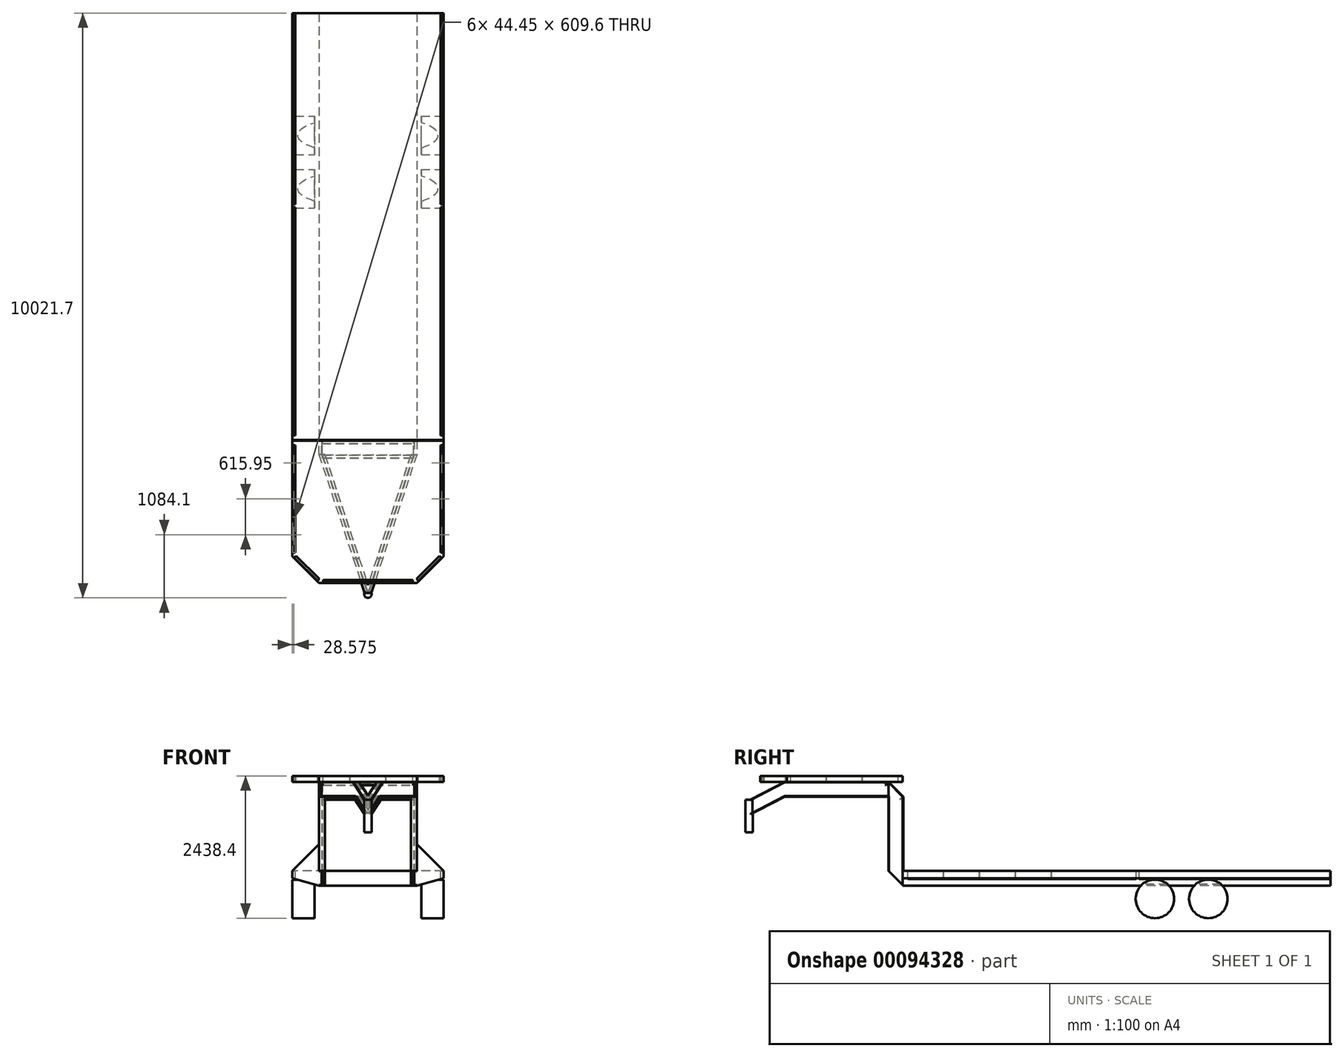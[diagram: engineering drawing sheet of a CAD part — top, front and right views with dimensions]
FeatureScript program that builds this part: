
annotation { "Feature Type Name" : "Feature", "Feature Type Description" : "" }
export const myFeature = defineFeature(function(context is Context, id is Id, definition is map)
    precondition{}
    {
        {
            var Q0;
            Q0=qCreatedBy(makeId("Front.planeOp"),FACE);
            var sketch = newSketch(context, id + "F0", { "sketchPlane" : qUnion([Q0])});
            skLineSegment(sketch, "E0.rect.bottom", {"start": v(1295.4, 812.8) * mm, "end": v(-1295.4, 812.8) * mm});
            skLineSegment(sketch, "E0.rect.top", {"start": v(1295.4, 558.8) * mm, "end": v(-1295.4, 558.8) * mm});
            skLineSegment(sketch, "E0.rect.left", {"start": v(1295.4, 812.8) * mm, "end": v(1295.4, 558.8) * mm});
            skLineSegment(sketch, "E0.rect.right", {"start": v(-1295.4, 812.8) * mm, "end": v(-1295.4, 558.8) * mm});
            skPoint(sketch, "E0.rect.middle", {"position": v(0, 685.8) * mm});
            skSolve(sketch);
        }
        {
            var Q0;
            Q0=qSketchRegion(id+"F0",true);
            extrude(context, id + "F1", {"entities" : qUnion([Q0]), "depth" : 7315.2 * mm});
        }
        {
            var Q0;
            {var subQ0=sQuery(id+"FU6Cp20yWSytbLJ_1.wireOp",EDGE,"516zEHSR-i4bq-akFn-s86x-5tDhRc9qmYIe");var subQ1=sQuery(id+"FU6Cp20yWSytbLJ_1.wireOp",EDGE,"pIKuKbnO-BRQA-nErB-13iL-2qYtMzEWX1Er");var subQ2=sQuery(id+"FU6Cp20yWSytbLJ_1.wireOp",EDGE,"PYxLWf9Y-Gqo5-IOfk-YQH7-kY8rKgNUq3Ly");var subQ3=sQuery(id+"FU6Cp20yWSytbLJ_1.wireOp",EDGE,"HUdA5PYD-mE7W-SRS9-FlNJ-WsRSMuGNaLoF");var subQ4=makeQuery(id+"FC5x2sPdwrUGjzl_1.opExtrude","CAP_FACE",FACE,{"disambiguationData":[OSD([subQ3,subQ2,subQ1,subQ0])],"isStart":true});var subQ5=sQuery(id+"FtYi234e1mes3no_1.wireOp",EDGE,"0333ae5e-be5c-4696-89fa-82c44326a229");var subQ6=makeQuery(id+"Fx2GEeHIH9ebrkq_1.opExtrude","CAP_FACE",FACE,{"disambiguationData":[OSD([subQ5])],"isStart":true});var subQ7=sQuery(id+"F0.wireOp",EDGE,"E0.rect.right");var subQ8=makeQuery(id+"FC5x2sPdwrUGjzl_1.opExtrude","CAP_FACE",FACE,{"disambiguationData":[OSD([subQ7])],"isStart":false});var subQ9=makeQuery(id+"F1.opExtrude","SWEPT_FACE",FACE,{"disambiguationData":[OSD([subQ7])]});var subQ10=sQuery(id+"FtYi234e1mes3no_1.wireOp",EDGE,"dfd4e7ae-838f-45d7-bc5a-27b7e8f56e23");var subQ11=sQuery(id+"F0.wireOp",EDGE,"E0.rect.left");var subQ12=makeQuery(id+"Fx2GEeHIH9ebrkq_1.opExtrude","CAP_FACE",FACE,{"disambiguationData":[OSD([subQ11,subQ3,subQ2,subQ1,subQ0]),ownerDisambiguation([makeQuery(id+"Fx2GEeHIH9ebrkq_1.opExtrude","SWEPT_BODY",BODY,{"disambiguationData":[OSD([subQ10])]})])],"isStart":false});var subQ13=makeQuery(id+"F1.opExtrude","SWEPT_FACE",FACE,{"disambiguationData":[OSD([subQ11])]});var subQ14=makeQuery(id+"Fx2GEeHIH9ebrkq_1.opExtrude","SWEPT_FACE",FACE,{"disambiguationData":[OSD([subQ5])]});var subQ15=makeQuery(id+"Fx2GEeHIH9ebrkq_1.opExtrude","CAP_FACE",FACE,{"disambiguationData":[OSD([subQ11,subQ3,subQ2,subQ1,subQ0]),ownerDisambiguation([makeQuery(id+"Fx2GEeHIH9ebrkq_1.opExtrude","SWEPT_BODY",BODY,{"disambiguationData":[OSD([subQ5])]})])],"isStart":false});var subQ16=makeQuery(id+"Fx2GEeHIH9ebrkq_1.opExtrude","SWEPT_FACE",FACE,{"disambiguationData":[OSD([subQ10])]});var subQ17=makeQuery(id+"Fx2GEeHIH9ebrkq_1.opExtrude","CAP_FACE",FACE,{"disambiguationData":[OSD([subQ10])],"isStart":true});var subQ18=sQuery(id+"F0.wireOp",EDGE,"E0.rect.top");var subQ19=makeQuery(id+"F1.opExtrude","SWEPT_FACE",FACE,{"disambiguationData":[OSD([subQ18])]});var subQ20=sQuery(id+"F0.wireOp",EDGE,"E0.rect.bottom");Q0=makeQuery(id+"FWcp0c4Uuyueshzcz_1.boolean.opBoolean","MERGE",FACE,{"derivedFrom":[makeQuery(id+"Fx2GEeHIH9ebrkq_1.boolean.opBoolean","SPLIT",FACE,{"disambiguationData":[TD([makeQuery(id+"F1.opExtrude","CAP_FACE",FACE,{"disambiguationData":[OSD([subQ20,subQ18,subQ11,subQ7])],"isStart":true}),subQ13,subQ9,subQ8,subQ4,subQ16,subQ17,subQ6,subQ12,subQ15])],"derivedFrom":subQ19}),makeQuery(id+"Fx2GEeHIH9ebrkq_1.boolean.opBoolean","SPLIT",FACE,{"disambiguationData":[TD([makeQuery(id+"F1.opExtrude","CAP_FACE",FACE,{"disambiguationData":[OSD([subQ20,subQ18,subQ11,subQ7])],"isStart":false}),subQ13,subQ9,subQ8,subQ4,subQ17,subQ14,subQ6,subQ12,subQ15])],"derivedFrom":subQ19}),makeQuery(id+"Fx2GEeHIH9ebrkq_1.boolean.opBoolean","SPLIT",FACE,{"disambiguationData":[TD([subQ13,subQ9,subQ8,subQ4,subQ16,subQ17,subQ14,subQ6,subQ12,subQ15])],"derivedFrom":subQ19}),makeQuery(id+"FWcp0c4Uuyueshzcz_1.opExtrude","SWEPT_FACE",FACE,{"disambiguationData":[OSD([sQuery(id+"FtVBCKT4kURnRFX_1.wireOp",EDGE,"0c15b902-9fc4-4e75-a3e0-c7f493582f48.bottom")])]})]});}
            var sketch = newSketch(context, id + "F2", { "sketchPlane" : qUnion([Q0])});
            skLineSegment(sketch, "E1", {"start": v(838.2, 7315.2) * mm, "end": v(838.2, 7324.72) * mm});
            skLineSegment(sketch, "E2", {"start": v(838.2, 7324.72) * mm, "end": v(792.16, 7324.72) * mm});
            skLineSegment(sketch, "E3", {"start": v(792.16, 7324.72) * mm, "end": v(792.16, 7559.68) * mm});
            skLineSegment(sketch, "E4", {"start": v(792.16, 7559.68) * mm, "end": v(838.2, 7559.68) * mm});
            skLineSegment(sketch, "E5", {"start": v(838.2, 7559.68) * mm, "end": v(838.2, 7569.2) * mm});
            skLineSegment(sketch, "E6", {"start": v(838.2, 7569.2) * mm, "end": v(736.6, 7569.2) * mm});
            skLineSegment(sketch, "E7", {"start": v(736.6, 7569.2) * mm, "end": v(736.6, 7559.68) * mm});
            skLineSegment(sketch, "E8", {"start": v(736.6, 7559.68) * mm, "end": v(782.64, 7559.68) * mm});
            skLineSegment(sketch, "E9", {"start": v(782.64, 7559.68) * mm, "end": v(782.64, 7324.72) * mm});
            skLineSegment(sketch, "E10", {"start": v(782.64, 7324.72) * mm, "end": v(736.6, 7324.72) * mm});
            skLineSegment(sketch, "E11", {"start": v(736.6, 7324.72) * mm, "end": v(736.6, 7315.2) * mm});
            skLineSegment(sketch, "E12", {"start": v(736.6, 7315.2) * mm, "end": v(838.2, 7315.2) * mm});
            skLineSegment(sketch, "E13", {"start": v(792.16, 7559.68) * mm, "end": v(782.64, 7559.68) * mm, "construction": true});
            skLineSegment(sketch, "E14", {"start": v(0, 7315.2) * mm, "end": v(0, 0) * mm, "construction": true});
            skLineSegment(sketch, "E15.MirrorCS", {"start": v(-792.16, 7559.68) * mm, "end": v(-782.64, 7559.68) * mm, "construction": true});
            skLineSegment(sketch, "E16.MirrorCS", {"start": v(-736.6, 7559.68) * mm, "end": v(-782.64, 7559.68) * mm});
            skLineSegment(sketch, "E17.MirrorCS", {"start": v(-736.6, 7569.2) * mm, "end": v(-736.6, 7559.68) * mm});
            skLineSegment(sketch, "E18.MirrorCS", {"start": v(-838.2, 7315.2) * mm, "end": v(-838.2, 7324.72) * mm});
            skLineSegment(sketch, "E19.MirrorCS", {"start": v(-792.16, 7559.68) * mm, "end": v(-838.2, 7559.68) * mm});
            skLineSegment(sketch, "E20.MirrorCS", {"start": v(-838.2, 7559.68) * mm, "end": v(-838.2, 7569.2) * mm});
            skLineSegment(sketch, "E21.MirrorCS", {"start": v(-838.2, 7569.2) * mm, "end": v(-736.6, 7569.2) * mm});
            skLineSegment(sketch, "E22.MirrorCS", {"start": v(-736.6, 7315.2) * mm, "end": v(-838.2, 7315.2) * mm});
            skLineSegment(sketch, "E23.MirrorCS", {"start": v(-736.6, 7324.72) * mm, "end": v(-736.6, 7315.2) * mm});
            skLineSegment(sketch, "E24.MirrorCS", {"start": v(-838.2, 7324.72) * mm, "end": v(-792.16, 7324.72) * mm});
            skLineSegment(sketch, "E25.MirrorCS", {"start": v(-782.64, 7324.72) * mm, "end": v(-736.6, 7324.72) * mm});
            skLineSegment(sketch, "E26.MirrorCS", {"start": v(-792.16, 7324.72) * mm, "end": v(-792.16, 7559.68) * mm});
            skLineSegment(sketch, "E27.MirrorCS", {"start": v(-782.64, 7559.68) * mm, "end": v(-782.64, 7324.72) * mm});
            skSolve(sketch);
        }
        {
            var Q0;
            Q0=makeQuery(id+"F2.imprint","IMPRINT",FACE,{"disambiguationData":[TD([[makeQuery(id+"F2.imprint","IMPRINT",EDGE,{"derivedFrom":sQuery(id+"F2.wireOp",EDGE,"E16.MirrorCS")}),-1.0]])]});
            var Q1;
            Q1=makeQuery(id+"F2.imprint","IMPRINT",FACE,{"disambiguationData":[TD([[makeQuery(id+"F2.imprint","IMPRINT",EDGE,{"derivedFrom":sQuery(id+"F2.wireOp",EDGE,"E1")}),1.0]])]});
            extrude(context, id + "F3", {"entities" : qUnion([Q0, Q1]), "operationType" : NewBodyOperationType.ADD, "oppositeDirection" : true, "depth" : 1524 * mm});
        }
        {
            var Q0;
            Q0=makeQuery(id+"F3.opExtrude","CAP_FACE",FACE,{"disambiguationData":[OSD([sQuery(id+"F2.wireOp",EDGE,"E1"),sQuery(id+"F2.wireOp",EDGE,"E2"),sQuery(id+"F2.wireOp",EDGE,"E3"),sQuery(id+"F2.wireOp",EDGE,"E4"),sQuery(id+"F2.wireOp",EDGE,"E5"),sQuery(id+"F2.wireOp",EDGE,"E6"),sQuery(id+"F2.wireOp",EDGE,"E7"),sQuery(id+"F2.wireOp",EDGE,"E8"),sQuery(id+"F2.wireOp",EDGE,"E9"),sQuery(id+"F2.wireOp",EDGE,"E10"),sQuery(id+"F2.wireOp",EDGE,"E11"),sQuery(id+"F2.wireOp",EDGE,"E12")])],"isStart":false});
            var sketch = newSketch(context, id + "F4", { "sketchPlane" : qUnion([Q0])});
            skLineSegment(sketch, "E28", {"start": v(-787.4, -7569.2) * mm, "end": v(-201.04, -9347.2) * mm});
            skLineSegment(sketch, "E29", {"start": v(-201.04, -9347.2) * mm, "end": v(0, -9956.8) * mm});
            skLineSegment(sketch, "E30", {"start": v(0, -9956.8) * mm, "end": v(201.04, -9347.2) * mm});
            skLineSegment(sketch, "E31", {"start": v(201.04, -9347.2) * mm, "end": v(787.4, -7569.2) * mm});
            skSolve(sketch);
        }
        {
            var Q0;
            {var subQ0=sQuery(id+"FU6Cp20yWSytbLJ_1.wireOp",EDGE,"pIKuKbnO-BRQA-nErB-13iL-2qYtMzEWX1Er");var subQ1=sQuery(id+"FU6Cp20yWSytbLJ_1.wireOp",EDGE,"PYxLWf9Y-Gqo5-IOfk-YQH7-kY8rKgNUq3Ly");var subQ2=sQuery(id+"FU6Cp20yWSytbLJ_1.wireOp",EDGE,"HUdA5PYD-mE7W-SRS9-FlNJ-WsRSMuGNaLoF");var subQ3=sQuery(id+"F0.wireOp",EDGE,"E0.rect.bottom");var subQ5=sQuery(id+"F0.wireOp",EDGE,"E0.rect.left");var subQ7=sQuery(id+"FU6Cp20yWSytbLJ_1.wireOp",EDGE,"516zEHSR-i4bq-akFn-s86x-5tDhRc9qmYIe");Q0=makeQuery(id+"FsKg1WZKStzT7it_1.boolean.opBoolean","SPLIT",FACE,{"disambiguationData":[TD([makeQuery(id+"F1.opExtrude","SWEPT_FACE",FACE,{"disambiguationData":[OSD([subQ3])]})])],"derivedFrom":makeQuery(id+"Fx2GEeHIH9ebrkq_1.boolean.opBoolean","MERGE",FACE,{"derivedFrom":[makeQuery(id+"FC5x2sPdwrUGjzl_1.boolean.opBoolean","MERGE",FACE,{"derivedFrom":[makeQuery(id+"F1.opExtrude","SWEPT_FACE",FACE,{"disambiguationData":[OSD([subQ5])]}),makeQuery(id+"FC5x2sPdwrUGjzl_1.opExtrude","CAP_FACE",FACE,{"disambiguationData":[OSD([subQ2,subQ1,subQ0,subQ7])],"isStart":true})]}),makeQuery(id+"Fx2GEeHIH9ebrkq_1.opExtrude","CAP_FACE",FACE,{"disambiguationData":[OSD([subQ5,subQ2,subQ1,subQ0,subQ7]),ownerDisambiguation([makeQuery(id+"Fx2GEeHIH9ebrkq_1.opExtrude","SWEPT_BODY",BODY,{"disambiguationData":[OSD([sQuery(id+"FtYi234e1mes3no_1.wireOp",EDGE,"dfd4e7ae-838f-45d7-bc5a-27b7e8f56e23")])]})])],"isStart":false}),makeQuery(id+"Fx2GEeHIH9ebrkq_1.opExtrude","CAP_FACE",FACE,{"disambiguationData":[OSD([subQ5,subQ2,subQ1,subQ0,subQ7]),ownerDisambiguation([makeQuery(id+"Fx2GEeHIH9ebrkq_1.opExtrude","SWEPT_BODY",BODY,{"disambiguationData":[OSD([sQuery(id+"FtYi234e1mes3no_1.wireOp",EDGE,"0333ae5e-be5c-4696-89fa-82c44326a229")])]})])],"isStart":false})]})});}
            var sketch = newSketch(context, id + "F5", { "sketchPlane" : qUnion([Q0])});
            skLineSegment(sketch, "E32", {"start": v(-7315.2, 558.8) * mm, "end": v(-7569.2, 812.8) * mm});
            skLineSegment(sketch, "E33", {"start": v(-7569.2, 812.8) * mm, "end": v(-7569.2, 558.8) * mm});
            skLineSegment(sketch, "E34", {"start": v(-7569.2, 558.8) * mm, "end": v(-7315.2, 558.8) * mm});
            skSolve(sketch);
        }
        {
            var Q0;
            Q0=makeQuery(id+"F5.imprint","IMPRINT",FACE,{"disambiguationData":[TD([[makeQuery(id+"F5.imprint","IMPRINT",EDGE,{"derivedFrom":sQuery(id+"F5.wireOp",EDGE,"E32")}),1.0]])]});
            extrude(context, id + "F6", {"entities" : qUnion([Q0]), "operationType" : NewBodyOperationType.REMOVE, "endBound" : BoundingType.THROUGH_ALL, "oppositeDirection" : true, "depth" : 25.4 * mm});
        }
        {
            var Q0;
            Q0=makeQuery(id+"F3.opExtrude","SWEPT_FACE",FACE,{"disambiguationData":[OSD([sQuery(id+"F2.wireOp",EDGE,"E6")])]});
            var sketch = newSketch(context, id + "F7", { "sketchPlane" : qUnion([Q0])});
            skLineSegment(sketch, "E35", {"start": v(736.6, 2082.8) * mm, "end": v(838.2, 2082.8) * mm});
            skLineSegment(sketch, "E36", {"start": v(838.2, 2082.8) * mm, "end": v(838.2, 2092.32) * mm});
            skLineSegment(sketch, "E37", {"start": v(838.2, 2092.32) * mm, "end": v(792.16, 2092.32) * mm});
            skLineSegment(sketch, "E38", {"start": v(792.16, 2092.32) * mm, "end": v(792.16, 2327.28) * mm});
            skLineSegment(sketch, "E39", {"start": v(792.16, 2327.28) * mm, "end": v(838.2, 2327.28) * mm});
            skLineSegment(sketch, "E40", {"start": v(838.2, 2327.28) * mm, "end": v(838.2, 2336.8) * mm});
            skLineSegment(sketch, "E41", {"start": v(838.2, 2336.8) * mm, "end": v(736.6, 2336.8) * mm});
            skLineSegment(sketch, "E42", {"start": v(736.6, 2336.8) * mm, "end": v(736.6, 2327.28) * mm});
            skLineSegment(sketch, "E43", {"start": v(736.6, 2327.28) * mm, "end": v(782.64, 2327.28) * mm});
            skLineSegment(sketch, "E44", {"start": v(782.64, 2327.28) * mm, "end": v(782.64, 2092.32) * mm});
            skLineSegment(sketch, "E45", {"start": v(782.64, 2092.32) * mm, "end": v(736.6, 2092.32) * mm});
            skLineSegment(sketch, "E46", {"start": v(736.6, 2092.32) * mm, "end": v(736.6, 2082.8) * mm});
            skLineSegment(sketch, "E47", {"start": v(782.64, 2092.32) * mm, "end": v(792.16, 2092.32) * mm, "construction": true});
            skLineSegment(sketch, "E48", {"start": v(0, 558.8) * mm, "end": v(0, 812.8) * mm, "construction": true});
            skLineSegment(sketch, "E49.MirrorCS", {"start": v(-782.64, 2092.32) * mm, "end": v(-792.16, 2092.32) * mm, "construction": true});
            skLineSegment(sketch, "E50.MirrorCS", {"start": v(-782.64, 2092.32) * mm, "end": v(-736.6, 2092.32) * mm});
            skLineSegment(sketch, "E51.MirrorCS", {"start": v(-736.6, 2092.32) * mm, "end": v(-736.6, 2082.8) * mm});
            skLineSegment(sketch, "E52.MirrorCS", {"start": v(-736.6, 2082.8) * mm, "end": v(-838.2, 2082.8) * mm});
            skLineSegment(sketch, "E53.MirrorCS", {"start": v(-838.2, 2082.8) * mm, "end": v(-838.2, 2092.32) * mm});
            skLineSegment(sketch, "E54.MirrorCS", {"start": v(-838.2, 2092.32) * mm, "end": v(-792.16, 2092.32) * mm});
            skLineSegment(sketch, "E55.MirrorCS", {"start": v(-792.16, 2327.28) * mm, "end": v(-838.2, 2327.28) * mm});
            skLineSegment(sketch, "E56.MirrorCS", {"start": v(-838.2, 2336.8) * mm, "end": v(-736.6, 2336.8) * mm});
            skLineSegment(sketch, "E57.MirrorCS", {"start": v(-736.6, 2327.28) * mm, "end": v(-782.64, 2327.28) * mm});
            skLineSegment(sketch, "E58.MirrorCS", {"start": v(-736.6, 2336.8) * mm, "end": v(-736.6, 2327.28) * mm});
            skLineSegment(sketch, "E59.MirrorCS", {"start": v(-838.2, 2327.28) * mm, "end": v(-838.2, 2336.8) * mm});
            skLineSegment(sketch, "E60.MirrorCS", {"start": v(-792.16, 2092.32) * mm, "end": v(-792.16, 2327.28) * mm});
            skLineSegment(sketch, "E61.MirrorCS", {"start": v(-782.64, 2327.28) * mm, "end": v(-782.64, 2092.32) * mm});
            skSolve(sketch);
        }
        {
            var Q1;
            Q1=makeQuery(id+"F4.imprint","IMPRINT",FACE,{"disambiguationData":[TD([[makeQuery(id+"F4.imprint","IMPRINT",EDGE,{"derivedFrom":makeQuery(id+"F3.opExtrude","CAP_EDGE",EDGE,{"disambiguationData":[OSD([sQuery(id+"F2.wireOp",EDGE,"E1")])],"isStart":false})}),-1.0]])]});
            var Q2;
            Q2=makeQuery(id+"F7.imprint","IMPRINT",FACE,{"disambiguationData":[TD([[makeQuery(id+"F7.imprint","IMPRINT",EDGE,{"derivedFrom":sQuery(id+"F7.wireOp",EDGE,"E35")}),-1.0]])]});
            var Q3;
            Q3=sQuery(id+"F7.wireOp",VERTEX,"E45.end");
            var Q4;
            Q4=makeQuery(id+"F3.opExtrude","CAP_VERTEX",VERTEX,{"disambiguationData":[OSD([sQuery(id+"F2.wireOp",EDGE,"E7"),sQuery(id+"F2.wireOp",EDGE,"E8")])],"isStart":false});
            loft(context, id + "F8", {"operationType" : NewBodyOperationType.ADD, "sheetProfilesArray" : [{ "sheetProfileEntities" : qUnion([Q1]) }, { "sheetProfileEntities" : qUnion([Q2]) }], "matchConnections" : true, "connections" : [{ "connectionEntities" : qUnion([Q3, Q4]), "connectionEdgeQueries" : qUnion([]), "connectionEdgeParameters" : [] }]});
        }
        {
            var Q1;
            Q1=makeQuery(id+"F7.imprint","IMPRINT",FACE,{"disambiguationData":[TD([[makeQuery(id+"F7.imprint","IMPRINT",EDGE,{"derivedFrom":sQuery(id+"F7.wireOp",EDGE,"E50.MirrorCS")}),-1.0]])]});
            var Q2;
            Q2=makeQuery(id+"F3.opExtrude","CAP_FACE",FACE,{"disambiguationData":[OSD([sQuery(id+"F2.wireOp",EDGE,"E16.MirrorCS"),sQuery(id+"F2.wireOp",EDGE,"E17.MirrorCS"),sQuery(id+"F2.wireOp",EDGE,"E18.MirrorCS"),sQuery(id+"F2.wireOp",EDGE,"E19.MirrorCS"),sQuery(id+"F2.wireOp",EDGE,"E20.MirrorCS"),sQuery(id+"F2.wireOp",EDGE,"E21.MirrorCS"),sQuery(id+"F2.wireOp",EDGE,"E22.MirrorCS"),sQuery(id+"F2.wireOp",EDGE,"E23.MirrorCS"),sQuery(id+"F2.wireOp",EDGE,"E24.MirrorCS"),sQuery(id+"F2.wireOp",EDGE,"E25.MirrorCS"),sQuery(id+"F2.wireOp",EDGE,"E26.MirrorCS"),sQuery(id+"F2.wireOp",EDGE,"E27.MirrorCS")])],"isStart":false});
            loft(context, id + "F9", {"operationType" : NewBodyOperationType.ADD, "sheetProfilesArray" : [{ "sheetProfileEntities" : qUnion([Q1]) }, { "sheetProfileEntities" : qUnion([Q2]) }]});
        }
        {
            var Q0;
            Q0=qSketchRegion(id+"F4",true);
            var Q1;
            Q1=makeQuery(id+"F7.imprint","IMPRINT",FACE,{"disambiguationData":[TD([[makeQuery(id+"F7.imprint","IMPRINT",EDGE,{"derivedFrom":sQuery(id+"F7.wireOp",EDGE,"E35")}),-1.0]])]});
            var Q2;
            Q2=sQuery(id+"F4.wireOp",EDGE,"E31");
            sweep(context, id + "F10", {"operationType" : NewBodyOperationType.ADD, "profiles" : qUnion([Q0, Q1]), "path" : qUnion([Q2]), "keepProfileOrientation" : true});
        }
        {
            var Q0;
            Q0=makeQuery(id+"F7.imprint","IMPRINT",FACE,{"disambiguationData":[TD([[makeQuery(id+"F7.imprint","IMPRINT",EDGE,{"derivedFrom":sQuery(id+"F7.wireOp",EDGE,"E50.MirrorCS")}),-1.0]])]});
            var Q1;
            Q1=sQuery(id+"F4.wireOp",EDGE,"E28");
            sweep(context, id + "F11", {"operationType" : NewBodyOperationType.ADD, "profiles" : qUnion([Q0]), "path" : qUnion([Q1]), "keepProfileOrientation" : true});
        }
        {
            var Q0;
            Q0=makeQuery(id+"F10.opSweep","SWEPT_FACE",FACE,{"disambiguationData":[OSD([sQuery(id+"F4.wireOp",EDGE,"E31"),sQuery(id+"F7.wireOp",EDGE,"E38")])]});
            var sketch = newSketch(context, id + "F12", { "sketchPlane" : qUnion([Q0])});
            skLineSegment(sketch, "E62", {"start": v(-8812.47, 2092.32) * mm, "end": v(-9455.86, 1778) * mm});
            skSolve(sketch);
        }
        {
            var Q0;
            Q0=makeQuery(id+"F10.opSweep","CAP_FACE",FACE,{"disambiguationData":[OSD([sQuery(id+"F4.wireOp",VERTEX,"E31.start"),sQuery(id+"F7.wireOp",EDGE,"E35"),sQuery(id+"F7.wireOp",EDGE,"E36"),sQuery(id+"F7.wireOp",EDGE,"E37"),sQuery(id+"F7.wireOp",EDGE,"E38"),sQuery(id+"F7.wireOp",EDGE,"E39"),sQuery(id+"F7.wireOp",EDGE,"E40"),sQuery(id+"F7.wireOp",EDGE,"E41"),sQuery(id+"F7.wireOp",EDGE,"E42"),sQuery(id+"F7.wireOp",EDGE,"E43"),sQuery(id+"F7.wireOp",EDGE,"E44"),sQuery(id+"F7.wireOp",EDGE,"E45"),sQuery(id+"F7.wireOp",EDGE,"E46")])],"isStart":false});
            var Q1;
            Q1=sQuery(id+"F12.wireOp",EDGE,"E62");
            sweep(context, id + "F13", {"operationType" : NewBodyOperationType.ADD, "profiles" : qUnion([Q0]), "path" : qUnion([Q1])});
        }
        {
            var Q0;
            Q0=makeQuery(id+"F11.opSweep","SWEPT_FACE",FACE,{"disambiguationData":[OSD([sQuery(id+"F4.wireOp",EDGE,"E28"),sQuery(id+"F7.wireOp",EDGE,"E60.MirrorCS")])]});
            var sketch = newSketch(context, id + "F14", { "sketchPlane" : qUnion([Q0])});
            skLineSegment(sketch, "E63", {"start": v(8812.47, 2092.32) * mm, "end": v(9455.86, 1778) * mm});
            skSolve(sketch);
        }
        {
            var Q0;
            Q0=makeQuery(id+"F11.opSweep","CAP_FACE",FACE,{"disambiguationData":[OSD([sQuery(id+"F4.wireOp",VERTEX,"E28.end"),sQuery(id+"F7.wireOp",EDGE,"E50.MirrorCS"),sQuery(id+"F7.wireOp",EDGE,"E51.MirrorCS"),sQuery(id+"F7.wireOp",EDGE,"E52.MirrorCS"),sQuery(id+"F7.wireOp",EDGE,"E53.MirrorCS"),sQuery(id+"F7.wireOp",EDGE,"E54.MirrorCS"),sQuery(id+"F7.wireOp",EDGE,"E55.MirrorCS"),sQuery(id+"F7.wireOp",EDGE,"E56.MirrorCS"),sQuery(id+"F7.wireOp",EDGE,"E57.MirrorCS"),sQuery(id+"F7.wireOp",EDGE,"E58.MirrorCS"),sQuery(id+"F7.wireOp",EDGE,"E59.MirrorCS"),sQuery(id+"F7.wireOp",EDGE,"E60.MirrorCS"),sQuery(id+"F7.wireOp",EDGE,"E61.MirrorCS")])],"isStart":false});
            var Q1;
            Q1=sQuery(id+"F14.wireOp",EDGE,"E63");
            sweep(context, id + "F15", {"operationType" : NewBodyOperationType.ADD, "profiles" : qUnion([Q0]), "path" : qUnion([Q1])});
        }
        {
            var Q0;
            {var subQ0=sQuery(id+"F2.wireOp",EDGE,"E9");Q0=makeQuery(id+"F8.boolean.opBoolean","MERGE",FACE,{"derivedFrom":[makeQuery(id+"F3.opExtrude","SWEPT_FACE",FACE,{"disambiguationData":[OSD([subQ0])]}),makeQuery(id+"F8.opLoft","SWEPT_FACE",FACE,{"disambiguationData":[OSD([sQuery(id+"F2.wireOp",EDGE,"E8"),subQ0,sQuery(id+"F2.wireOp",EDGE,"E10"),sQuery(id+"F7.wireOp",EDGE,"E43"),sQuery(id+"F7.wireOp",EDGE,"E44"),sQuery(id+"F7.wireOp",EDGE,"E45")])]})]});}
            var sketch = newSketch(context, id + "F16", { "sketchPlane" : qUnion([Q0])});
            skLineSegment(sketch, "E64", {"start": v(7369.08, 2028.92) * mm, "end": v(7315.2, 2082.8) * mm});
            skLineSegment(sketch, "E65", {"start": v(7315.2, 2082.8) * mm, "end": v(7569.2, 2336.8) * mm});
            skLineSegment(sketch, "E66", {"start": v(7569.2, 2336.8) * mm, "end": v(7623.08, 2282.92) * mm});
            skLineSegment(sketch, "E67", {"start": v(7623.08, 2282.92) * mm, "end": v(7616.35, 2276.18) * mm});
            skLineSegment(sketch, "E68", {"start": v(7616.35, 2276.18) * mm, "end": v(7573.96, 2318.57) * mm});
            skLineSegment(sketch, "E69", {"start": v(7573.96, 2318.57) * mm, "end": v(7333.43, 2078.04) * mm});
            skLineSegment(sketch, "E70", {"start": v(7333.43, 2078.04) * mm, "end": v(7375.82, 2035.65) * mm});
            skLineSegment(sketch, "E71", {"start": v(7375.82, 2035.65) * mm, "end": v(7369.08, 2028.92) * mm});
            skLineSegment(sketch, "E72", {"start": v(7453.7, 2198.3) * mm, "end": v(7446.96, 2205.04) * mm, "construction": true});
            skSolve(sketch);
        }
        {
            var Q0;
            Q0=qSketchRegion(id+"F16",true);
            var Q1;
            {var subQ0=sQuery(id+"F2.wireOp",EDGE,"E27.MirrorCS");Q1=makeQuery(id+"F9.boolean.opBoolean","MERGE",FACE,{"derivedFrom":[makeQuery(id+"F3.opExtrude","SWEPT_FACE",FACE,{"disambiguationData":[OSD([subQ0])]}),makeQuery(id+"F9.opLoft","SWEPT_FACE",FACE,{"disambiguationData":[OSD([sQuery(id+"F2.wireOp",EDGE,"E16.MirrorCS"),sQuery(id+"F2.wireOp",EDGE,"E25.MirrorCS"),subQ0,sQuery(id+"F7.wireOp",EDGE,"E50.MirrorCS"),sQuery(id+"F7.wireOp",EDGE,"E57.MirrorCS"),sQuery(id+"F7.wireOp",EDGE,"E61.MirrorCS")])]})]});}
            extrude(context, id + "F17", {"entities" : qUnion([Q0]), "operationType" : NewBodyOperationType.ADD, "endBound" : BoundingType.UP_TO_SURFACE, "endBoundEntityFace" : qUnion([Q1]), "depth" : 25.4 * mm});
        }
        {
            var Q0;
            {var subQ0=sQuery(id+"F0.wireOp",EDGE,"E0.rect.left");var subQ2=sQuery(id+"F0.wireOp",EDGE,"E0.rect.top");var subQ4=sQuery(id+"F0.wireOp",EDGE,"E0.rect.bottom");Q0=makeQuery(id+"F3.boolean.opBoolean","SPLIT",FACE,{"disambiguationData":[TD([makeQuery(id+"F1.opExtrude","SWEPT_FACE",FACE,{"disambiguationData":[OSD([subQ0])]})])],"derivedFrom":makeQuery(id+"F1.opExtrude","CAP_FACE",FACE,{"disambiguationData":[OSD([subQ4,subQ2,subQ0,sQuery(id+"F0.wireOp",EDGE,"E0.rect.right")])],"isStart":false})});}
            var sketch = newSketch(context, id + "F18", { "sketchPlane" : qUnion([Q0])});
            skLineSegment(sketch, "E73", {"start": v(1295.4, 812.8) * mm, "end": v(838.2, 1270) * mm});
            skLineSegment(sketch, "E74", {"start": v(838.2, 1270) * mm, "end": v(838.2, 812.8) * mm});
            skLineSegment(sketch, "E75", {"start": v(838.2, 812.8) * mm, "end": v(1295.4, 812.8) * mm, "construction": true});
            skLineSegment(sketch, "E76", {"start": v(-1295.4, 812.8) * mm, "end": v(-838.2, 812.8) * mm, "construction": true});
            skLineSegment(sketch, "E77", {"start": v(-838.2, 812.8) * mm, "end": v(-838.2, 1270) * mm});
            skLineSegment(sketch, "E78", {"start": v(-838.2, 1270) * mm, "end": v(-1295.4, 812.8) * mm});
            skLineSegment(sketch, "E79", {"start": v(1295.4, 812.8) * mm, "end": v(1295.4, 558.8) * mm});
            skLineSegment(sketch, "E80", {"start": v(1295.4, 558.8) * mm, "end": v(838.2, 558.8) * mm});
            skLineSegment(sketch, "E81", {"start": v(838.2, 558.8) * mm, "end": v(838.2, 812.8) * mm});
            skLineSegment(sketch, "E82", {"start": v(-1295.4, 812.8) * mm, "end": v(-1295.4, 558.8) * mm});
            skLineSegment(sketch, "E83", {"start": v(-1295.4, 558.8) * mm, "end": v(-838.2, 558.8) * mm});
            skLineSegment(sketch, "E84", {"start": v(-838.2, 558.8) * mm, "end": v(-838.2, 812.8) * mm});
            skSolve(sketch);
        }
        {
            var Q0;
            Q0=qSketchRegion(id+"F18",true);
            extrude(context, id + "F19", {"entities" : qUnion([Q0]), "operationType" : NewBodyOperationType.ADD, "depth" : 9.52 * mm});
        }
        {
            var Q0;
            Q0=makeQuery(id+"F11.boolean.opBoolean","MERGE",FACE,{"derivedFrom":[makeQuery(id+"F10.opSweep","SWEPT_FACE",FACE,{"disambiguationData":[OSD([sQuery(id+"F4.wireOp",EDGE,"E31"),sQuery(id+"F7.wireOp",EDGE,"E41")])]}),makeQuery(id+"F11.opSweep","SWEPT_FACE",FACE,{"disambiguationData":[OSD([sQuery(id+"F4.wireOp",EDGE,"E28"),sQuery(id+"F7.wireOp",EDGE,"E56.MirrorCS")])]})]});
            var sketch = newSketch(context, id + "F20", { "sketchPlane" : qUnion([Q0])});
            skLineSegment(sketch, "E85", {"start": v(1295.4, -7324.72) * mm, "end": v(-1295.4, -7324.72) * mm});
            skLineSegment(sketch, "E86", {"start": v(-1295.4, -7324.73) * mm, "end": v(-1295.4, -9305.93) * mm});
            skLineSegment(sketch, "E87", {"start": v(-1295.4, -9305.93) * mm, "end": v(-838.2, -9763.12) * mm});
            skLineSegment(sketch, "E88", {"start": v(-838.2, -9763.12) * mm, "end": v(838.2, -9763.12) * mm});
            skLineSegment(sketch, "E89", {"start": v(838.2, -9763.12) * mm, "end": v(1295.4, -9305.93) * mm});
            skLineSegment(sketch, "E90", {"start": v(1295.4, -9305.93) * mm, "end": v(1295.4, -7324.73) * mm});
            skSolve(sketch);
        }
        {
            var Q0;
            Q0=qSketchRegion(id+"F20",true);
            extrude(context, id + "F21", {"entities" : qUnion([Q0]), "depth" : 101.6 * mm});
        }
        {
            var Q0;
            Q0=makeQuery(id+"F19.boolean.opBoolean","MERGE",FACE,{"derivedFrom":[makeQuery(id+"F3.boolean.opBoolean","MERGE",FACE,{"derivedFrom":[makeQuery(id+"F1.opExtrude","SWEPT_FACE",FACE,{"disambiguationData":[OSD([sQuery(id+"F0.wireOp",EDGE,"E0.rect.top")])]}),makeQuery(id+"F3.opExtrude","CAP_FACE",FACE,{"disambiguationData":[OSD([sQuery(id+"F2.wireOp",EDGE,"E1"),sQuery(id+"F2.wireOp",EDGE,"E2"),sQuery(id+"F2.wireOp",EDGE,"E3"),sQuery(id+"F2.wireOp",EDGE,"E4"),sQuery(id+"F2.wireOp",EDGE,"E5"),sQuery(id+"F2.wireOp",EDGE,"E6"),sQuery(id+"F2.wireOp",EDGE,"E7"),sQuery(id+"F2.wireOp",EDGE,"E8"),sQuery(id+"F2.wireOp",EDGE,"E9"),sQuery(id+"F2.wireOp",EDGE,"E10"),sQuery(id+"F2.wireOp",EDGE,"E11"),sQuery(id+"F2.wireOp",EDGE,"E12")])],"isStart":true}),makeQuery(id+"F3.opExtrude","CAP_FACE",FACE,{"disambiguationData":[OSD([sQuery(id+"F2.wireOp",EDGE,"E16.MirrorCS"),sQuery(id+"F2.wireOp",EDGE,"E17.MirrorCS"),sQuery(id+"F2.wireOp",EDGE,"E18.MirrorCS"),sQuery(id+"F2.wireOp",EDGE,"E19.MirrorCS"),sQuery(id+"F2.wireOp",EDGE,"E20.MirrorCS"),sQuery(id+"F2.wireOp",EDGE,"E21.MirrorCS"),sQuery(id+"F2.wireOp",EDGE,"E22.MirrorCS"),sQuery(id+"F2.wireOp",EDGE,"E23.MirrorCS"),sQuery(id+"F2.wireOp",EDGE,"E24.MirrorCS"),sQuery(id+"F2.wireOp",EDGE,"E25.MirrorCS"),sQuery(id+"F2.wireOp",EDGE,"E26.MirrorCS"),sQuery(id+"F2.wireOp",EDGE,"E27.MirrorCS")])],"isStart":true})]}),makeQuery(id+"F19.opExtrude","SWEPT_FACE",FACE,{"disambiguationData":[OSD([sQuery(id+"F18.wireOp",EDGE,"E80")])]}),makeQuery(id+"F19.opExtrude","SWEPT_FACE",FACE,{"disambiguationData":[OSD([sQuery(id+"F18.wireOp",EDGE,"E83")])]})]});
            var sketch = newSketch(context, id + "F22", { "sketchPlane" : qUnion([Q0])});
            skCircle(sketch, "E91", {"center": v(0, 9958.22) * mm, "radius": 63.5 * mm});
            skSolve(sketch);
        }
        {
            var Q0;
            Q0=makeQuery(id+"F22.imprint","IMPRINT",FACE,{"disambiguationData":[TD([[makeQuery(id+"F22.imprint","IMPRINT",EDGE,{"derivedFrom":sQuery(id+"F22.wireOp",EDGE,"E91")}),1.0]])]});
            extrude(context, id + "F23", {"entities" : qUnion([Q0]), "operationType" : NewBodyOperationType.ADD, "oppositeDirection" : true, "depth" : 1473.2 * mm, "hasSecondDirection" : true, "secondDirectionOppositeDirection" : true, "secondDirectionDepth" : 914.4 * mm});
        }
        {
            var Q0;
            Q0=makeQuery(id+"F21.opExtrude","CAP_FACE",FACE,{"disambiguationData":[OSD([sQuery(id+"F20.wireOp",EDGE,"E85"),sQuery(id+"F20.wireOp",EDGE,"E86"),sQuery(id+"F20.wireOp",EDGE,"E87"),sQuery(id+"F20.wireOp",EDGE,"E88"),sQuery(id+"F20.wireOp",EDGE,"E89"),sQuery(id+"F20.wireOp",EDGE,"E90")])],"isStart":false});
            var sketch = newSketch(context, id + "F24", { "sketchPlane" : qUnion([Q0])});
            skLineSegment(sketch, "E92.0", {"start": v(1289.05, -9303.3) * mm, "end": v(1289.05, -3327.4) * mm});
            skLineSegment(sketch, "E92.1", {"start": v(-1289.05, -3327.4) * mm, "end": v(-1289.05, -9303.3) * mm});
            skLineSegment(sketch, "E92.2", {"start": v(-1289.05, -9303.3) * mm, "end": v(-835.57, -9756.77) * mm});
            skLineSegment(sketch, "E92.3", {"start": v(-835.57, -9756.77) * mm, "end": v(835.57, -9756.77) * mm});
            skLineSegment(sketch, "E92.4", {"start": v(835.57, -9756.77) * mm, "end": v(1289.05, -9303.3) * mm});
            skLineSegment(sketch, "E93", {"start": v(1289.05, -3276.6) * mm, "end": v(1289.05, -12.7) * mm});
            skLineSegment(sketch, "E94", {"start": v(-1244.6, -12.7) * mm, "end": v(-1244.6, -3276.6) * mm});
            skLineSegment(sketch, "E95", {"start": v(-1244.6, -12.7) * mm, "end": v(-1289.05, -12.7) * mm});
            skLineSegment(sketch, "E96", {"start": v(-1289.05, -12.7) * mm, "end": v(-1289.05, -3276.6) * mm});
            skLineSegment(sketch, "E97", {"start": v(-1289.05, -3276.6) * mm, "end": v(-1244.6, -3276.6) * mm});
            skLineSegment(sketch, "E98", {"start": v(1289.05, -3276.6) * mm, "end": v(1244.6, -3276.6) * mm});
            skLineSegment(sketch, "E99", {"start": v(1244.6, -3276.6) * mm, "end": v(1244.6, -12.7) * mm});
            skLineSegment(sketch, "E100", {"start": v(1244.6, -12.7) * mm, "end": v(1289.05, -12.7) * mm});
            skLineSegment(sketch, "E101", {"start": v(-1289.05, -3327.4) * mm, "end": v(-1244.6, -3327.4) * mm});
            skLineSegment(sketch, "E102", {"start": v(-1244.6, -3327.4) * mm, "end": v(-1244.6, -9284.88) * mm});
            skLineSegment(sketch, "E103", {"start": v(-1244.6, -9284.88) * mm, "end": v(-817.16, -9712.32) * mm});
            skLineSegment(sketch, "E104", {"start": v(-817.16, -9712.32) * mm, "end": v(817.16, -9712.32) * mm});
            skLineSegment(sketch, "E105", {"start": v(817.16, -9712.33) * mm, "end": v(1244.6, -9284.88) * mm});
            skLineSegment(sketch, "E106", {"start": v(1244.6, -9284.88) * mm, "end": v(1244.6, -3327.4) * mm});
            skLineSegment(sketch, "E107", {"start": v(1244.6, -3327.4) * mm, "end": v(1289.05, -3327.4) * mm});
            skLineSegment(sketch, "E108", {"start": v(-1244.6, -9284.88) * mm, "end": v(-1289.05, -9284.88) * mm, "construction": true});
            skLineSegment(sketch, "E109", {"start": v(-1030.88, -9498.6) * mm, "end": v(-1062.3, -9530.03) * mm, "construction": true});
            skLineSegment(sketch, "E110", {"start": v(0, -9712.32) * mm, "end": v(0, -9756.77) * mm, "construction": true});
            skLineSegment(sketch, "E111", {"start": v(1030.88, -9498.6) * mm, "end": v(1062.3, -9530.03) * mm, "construction": true});
            skLineSegment(sketch, "E112", {"start": v(-1244.6, -4781.55) * mm, "end": v(-1289.05, -4781.55) * mm});
            skLineSegment(sketch, "E113", {"start": v(-1244.6, -5397.5) * mm, "end": v(-1289.05, -5397.5) * mm});
            skLineSegment(sketch, "E114", {"start": v(-1244.6, -6013.45) * mm, "end": v(-1289.05, -6013.45) * mm});
            skLineSegment(sketch, "E115", {"start": v(-1244.6, -6629.4) * mm, "end": v(-1289.05, -6629.4) * mm});
            skLineSegment(sketch, "E116", {"start": v(-1244.6, -7239) * mm, "end": v(-1289.05, -7239) * mm});
            skLineSegment(sketch, "E117", {"start": v(-1244.6, -6623.05) * mm, "end": v(-1289.05, -6623.05) * mm});
            skLineSegment(sketch, "E118", {"start": v(-1244.6, -6007.1) * mm, "end": v(-1289.05, -6007.1) * mm});
            skLineSegment(sketch, "E119", {"start": v(-1244.6, -5391.15) * mm, "end": v(-1289.05, -5391.15) * mm});
            skLineSegment(sketch, "E120", {"start": v(-1244.6, -4775.2) * mm, "end": v(-1289.05, -4775.2) * mm});
            skLineSegment(sketch, "E121", {"start": v(-1289.05, -7400.92) * mm, "end": v(-1244.6, -7400.92) * mm});
            skLineSegment(sketch, "E122", {"start": v(-1289.05, -8010.52) * mm, "end": v(-1244.6, -8010.52) * mm});
            skLineSegment(sketch, "E123", {"start": v(-1289.05, -8016.87) * mm, "end": v(-1244.6, -8016.87) * mm});
            skLineSegment(sketch, "E124", {"start": v(-1289.05, -8626.47) * mm, "end": v(-1244.6, -8626.47) * mm});
            skLineSegment(sketch, "E125", {"start": v(-1289.05, -8632.82) * mm, "end": v(-1244.6, -8632.82) * mm});
            skLineSegment(sketch, "E126", {"start": v(-1244.6, -9242.42) * mm, "end": v(-1289.05, -9242.42) * mm});
            skLineSegment(sketch, "E127", {"start": v(-1228.44, -9301.04) * mm, "end": v(-1259.88, -9332.47) * mm});
            skLineSegment(sketch, "E128", {"start": v(-833.31, -9696.17) * mm, "end": v(-864.74, -9727.6) * mm});
            skLineSegment(sketch, "E129", {"start": v(-1259.88, -9332.47) * mm, "end": v(-1030.88, -9498.6) * mm, "construction": true});
            skLineSegment(sketch, "E130", {"start": v(-864.74, -9727.6) * mm, "end": v(-1030.88, -9498.6) * mm, "construction": true});
            skLineSegment(sketch, "E131", {"start": v(-768.35, -9712.32) * mm, "end": v(-768.35, -9756.77) * mm});
            skLineSegment(sketch, "E132", {"start": v(-311.15, -9756.77) * mm, "end": v(-311.15, -9712.32) * mm});
            skLineSegment(sketch, "E133", {"start": v(-304.8, -9756.77) * mm, "end": v(-304.8, -9712.32) * mm});
            skLineSegment(sketch, "E134", {"start": v(304.8, -9712.32) * mm, "end": v(304.8, -9756.77) * mm});
            skLineSegment(sketch, "E135", {"start": v(311.15, -9712.32) * mm, "end": v(311.15, -9756.77) * mm});
            skLineSegment(sketch, "E136", {"start": v(768.35, -9712.32) * mm, "end": v(768.35, -9756.77) * mm});
            skLineSegment(sketch, "E137", {"start": v(768.35, -9712.33) * mm, "end": v(835.57, -9756.77) * mm, "construction": true});
            skLineSegment(sketch, "E138", {"start": v(311.15, -9756.77) * mm, "end": v(768.35, -9712.33) * mm, "construction": true});
            skLineSegment(sketch, "E139", {"start": v(-768.35, -9712.33) * mm, "end": v(-311.15, -9756.77) * mm, "construction": true});
            skLineSegment(sketch, "E140", {"start": v(-768.35, -9712.33) * mm, "end": v(-835.57, -9756.77) * mm, "construction": true});
            skLineSegment(sketch, "E141", {"start": v(833.31, -9696.17) * mm, "end": v(864.74, -9727.6) * mm});
            skLineSegment(sketch, "E142", {"start": v(1228.44, -9301.04) * mm, "end": v(1259.88, -9332.47) * mm});
            skLineSegment(sketch, "E143", {"start": v(864.74, -9727.6) * mm, "end": v(1030.88, -9498.6) * mm, "construction": true});
            skLineSegment(sketch, "E144", {"start": v(1259.88, -9332.47) * mm, "end": v(1030.88, -9498.6) * mm, "construction": true});
            skLineSegment(sketch, "E145", {"start": v(1244.6, -9242.42) * mm, "end": v(1289.05, -9242.42) * mm});
            skLineSegment(sketch, "E146", {"start": v(1244.6, -8632.82) * mm, "end": v(1289.05, -8632.82) * mm});
            skLineSegment(sketch, "E147", {"start": v(1244.6, -8626.47) * mm, "end": v(1289.05, -8626.47) * mm});
            skLineSegment(sketch, "E148", {"start": v(1244.6, -8016.87) * mm, "end": v(1289.05, -8016.87) * mm});
            skLineSegment(sketch, "E149", {"start": v(1244.6, -8010.52) * mm, "end": v(1289.05, -8010.52) * mm});
            skLineSegment(sketch, "E150", {"start": v(1244.6, -7400.92) * mm, "end": v(1289.05, -7400.92) * mm});
            skLineSegment(sketch, "E151", {"start": v(1244.6, -7239) * mm, "end": v(1289.05, -7239) * mm});
            skLineSegment(sketch, "E152", {"start": v(1244.6, -6629.4) * mm, "end": v(1289.05, -6629.4) * mm});
            skLineSegment(sketch, "E153", {"start": v(1244.6, -6623.05) * mm, "end": v(1289.05, -6623.05) * mm});
            skLineSegment(sketch, "E154", {"start": v(1244.6, -6013.45) * mm, "end": v(1289.05, -6013.45) * mm});
            skLineSegment(sketch, "E155", {"start": v(1244.6, -6007.1) * mm, "end": v(1289.05, -6007.1) * mm});
            skLineSegment(sketch, "E156", {"start": v(1244.6, -5397.5) * mm, "end": v(1289.05, -5397.5) * mm});
            skLineSegment(sketch, "E157", {"start": v(1244.6, -5391.15) * mm, "end": v(1289.05, -5391.15) * mm});
            skLineSegment(sketch, "E158", {"start": v(1244.6, -4781.55) * mm, "end": v(1289.05, -4781.55) * mm});
            skLineSegment(sketch, "E159", {"start": v(1244.6, -4775.2) * mm, "end": v(1289.05, -4775.2) * mm});
            skSolve(sketch);
        }
        {
            var Q0;
            {var subQ0=sQuery(id+"F24.wireOp",EDGE,"E131");Q0=makeQuery(id+"F24.imprint","IMPRINT",FACE,{"disambiguationData":[TD([[makeQuery(id+"F24.imprint","IMPRINT",EDGE,{"derivedFrom":subQ0}),1.0]])]});}
            var Q1;
            {var subQ0=sQuery(id+"F24.wireOp",EDGE,"E135");Q1=makeQuery(id+"F24.imprint","IMPRINT",FACE,{"disambiguationData":[TD([[makeQuery(id+"F24.imprint","IMPRINT",EDGE,{"derivedFrom":subQ0}),1.0]])]});}
            var Q2;
            {var subQ0=sQuery(id+"F24.wireOp",EDGE,"E141");Q2=makeQuery(id+"F24.imprint","IMPRINT",FACE,{"disambiguationData":[TD([[makeQuery(id+"F24.imprint","IMPRINT",EDGE,{"derivedFrom":subQ0}),1.0]])]});}
            var Q3;
            {var subQ0=sQuery(id+"F24.wireOp",EDGE,"E145");Q3=makeQuery(id+"F24.imprint","IMPRINT",FACE,{"disambiguationData":[TD([[makeQuery(id+"F24.imprint","IMPRINT",EDGE,{"derivedFrom":subQ0}),1.0]])]});}
            var Q4;
            {var subQ0=sQuery(id+"F24.wireOp",EDGE,"E147");Q4=makeQuery(id+"F24.imprint","IMPRINT",FACE,{"disambiguationData":[TD([[makeQuery(id+"F24.imprint","IMPRINT",EDGE,{"derivedFrom":subQ0}),1.0]])]});}
            var Q5;
            {var subQ0=sQuery(id+"F24.wireOp",EDGE,"E149");Q5=makeQuery(id+"F24.imprint","IMPRINT",FACE,{"disambiguationData":[TD([[makeQuery(id+"F24.imprint","IMPRINT",EDGE,{"derivedFrom":subQ0}),1.0]])]});}
            var Q6;
            {var subQ0=sQuery(id+"F24.wireOp",EDGE,"E151");Q6=makeQuery(id+"F24.imprint","IMPRINT",FACE,{"disambiguationData":[TD([[makeQuery(id+"F24.imprint","IMPRINT",EDGE,{"derivedFrom":subQ0}),1.0]])]});}
            var Q7;
            {var subQ0=sQuery(id+"F24.wireOp",EDGE,"E153");Q7=makeQuery(id+"F24.imprint","IMPRINT",FACE,{"disambiguationData":[TD([[makeQuery(id+"F24.imprint","IMPRINT",EDGE,{"derivedFrom":subQ0}),1.0]])]});}
            var Q8;
            {var subQ0=sQuery(id+"F24.wireOp",EDGE,"E155");Q8=makeQuery(id+"F24.imprint","IMPRINT",FACE,{"disambiguationData":[TD([[makeQuery(id+"F24.imprint","IMPRINT",EDGE,{"derivedFrom":subQ0}),1.0]])]});}
            var Q9;
            {var subQ0=sQuery(id+"F24.wireOp",EDGE,"E157");Q9=makeQuery(id+"F24.imprint","IMPRINT",FACE,{"disambiguationData":[TD([[makeQuery(id+"F24.imprint","IMPRINT",EDGE,{"derivedFrom":subQ0}),1.0]])]});}
            var Q10;
            {var subQ0=sQuery(id+"F24.wireOp",EDGE,"E107");Q10=makeQuery(id+"F24.imprint","IMPRINT",FACE,{"disambiguationData":[TD([[makeQuery(id+"F24.imprint","IMPRINT",EDGE,{"derivedFrom":subQ0}),-1.0]])]});}
            var Q11;
            Q11=makeQuery(id+"F24.imprint","IMPRINT",FACE,{"disambiguationData":[TD([[makeQuery(id+"F24.imprint","IMPRINT",EDGE,{"derivedFrom":sQuery(id+"F24.wireOp",EDGE,"E93")}),1.0]])]});
            var Q12;
            Q12=makeQuery(id+"F24.imprint","IMPRINT",FACE,{"disambiguationData":[TD([[makeQuery(id+"F24.imprint","IMPRINT",EDGE,{"derivedFrom":sQuery(id+"F24.wireOp",EDGE,"E94")}),-1.0]])]});
            var Q13;
            {var subQ0=sQuery(id+"F24.wireOp",EDGE,"E101");Q13=makeQuery(id+"F24.imprint","IMPRINT",FACE,{"disambiguationData":[TD([[makeQuery(id+"F24.imprint","IMPRINT",EDGE,{"derivedFrom":subQ0}),-1.0]])]});}
            var Q14;
            {var subQ0=sQuery(id+"F24.wireOp",EDGE,"E112");Q14=makeQuery(id+"F24.imprint","IMPRINT",FACE,{"disambiguationData":[TD([[makeQuery(id+"F24.imprint","IMPRINT",EDGE,{"derivedFrom":subQ0}),1.0]])]});}
            var Q15;
            {var subQ0=sQuery(id+"F24.wireOp",EDGE,"E113");Q15=makeQuery(id+"F24.imprint","IMPRINT",FACE,{"disambiguationData":[TD([[makeQuery(id+"F24.imprint","IMPRINT",EDGE,{"derivedFrom":subQ0}),1.0]])]});}
            var Q16;
            {var subQ0=sQuery(id+"F24.wireOp",EDGE,"E114");Q16=makeQuery(id+"F24.imprint","IMPRINT",FACE,{"disambiguationData":[TD([[makeQuery(id+"F24.imprint","IMPRINT",EDGE,{"derivedFrom":subQ0}),1.0]])]});}
            var Q17;
            {var subQ0=sQuery(id+"F24.wireOp",EDGE,"E115");Q17=makeQuery(id+"F24.imprint","IMPRINT",FACE,{"disambiguationData":[TD([[makeQuery(id+"F24.imprint","IMPRINT",EDGE,{"derivedFrom":subQ0}),1.0]])]});}
            var Q18;
            {var subQ0=sQuery(id+"F24.wireOp",EDGE,"E121");Q18=makeQuery(id+"F24.imprint","IMPRINT",FACE,{"disambiguationData":[TD([[makeQuery(id+"F24.imprint","IMPRINT",EDGE,{"derivedFrom":subQ0}),-1.0]])]});}
            var Q19;
            {var subQ0=sQuery(id+"F24.wireOp",EDGE,"E123");Q19=makeQuery(id+"F24.imprint","IMPRINT",FACE,{"disambiguationData":[TD([[makeQuery(id+"F24.imprint","IMPRINT",EDGE,{"derivedFrom":subQ0}),-1.0]])]});}
            var Q20;
            {var subQ0=sQuery(id+"F24.wireOp",EDGE,"E125");Q20=makeQuery(id+"F24.imprint","IMPRINT",FACE,{"disambiguationData":[TD([[makeQuery(id+"F24.imprint","IMPRINT",EDGE,{"derivedFrom":subQ0}),-1.0]])]});}
            var Q21;
            {var subQ0=sQuery(id+"F24.wireOp",EDGE,"E127");Q21=makeQuery(id+"F24.imprint","IMPRINT",FACE,{"disambiguationData":[TD([[makeQuery(id+"F24.imprint","IMPRINT",EDGE,{"derivedFrom":subQ0}),1.0]])]});}
            extrude(context, id + "F25", {"entities" : qUnion([Q0, Q1, Q2, Q3, Q4, Q5, Q6, Q7, Q8, Q9, Q10, Q11, Q12, Q13, Q14, Q15, Q16, Q17, Q18, Q19, Q20, Q21]), "operationType" : NewBodyOperationType.REMOVE, "endBound" : BoundingType.THROUGH_ALL, "oppositeDirection" : true, "depth" : 25.4 * mm});
        }
        {
            var Q0;
            {var subQ0=sQuery(id+"F24.wireOp",EDGE,"E133");Q0=makeQuery(id+"F24.imprint","IMPRINT",FACE,{"disambiguationData":[TD([[makeQuery(id+"F24.imprint","IMPRINT",EDGE,{"derivedFrom":subQ0}),-1.0]])]});}
            extrude(context, id + "F26", {"entities" : qUnion([Q0]), "operationType" : NewBodyOperationType.REMOVE, "endBound" : BoundingType.UP_TO_NEXT, "oppositeDirection" : true, "depth" : 25.4 * mm});
        }
        {
            var Q0;
            Q0=makeQuery(id+"F19.boolean.opBoolean","MERGE",FACE,{"derivedFrom":[makeQuery(id+"F3.opExtrude","SWEPT_FACE",FACE,{"disambiguationData":[OSD([sQuery(id+"F2.wireOp",EDGE,"E2")])]}),makeQuery(id+"F19.opExtrude","CAP_FACE",FACE,{"disambiguationData":[OSD([sQuery(id+"F18.wireOp",EDGE,"E73"),sQuery(id+"F18.wireOp",EDGE,"E74"),sQuery(id+"F18.wireOp",EDGE,"E79"),sQuery(id+"F18.wireOp",EDGE,"E80"),sQuery(id+"F18.wireOp",EDGE,"E81")])],"isStart":false})]});
            var sketch = newSketch(context, id + "F27", { "sketchPlane" : qUnion([Q0])});
            skLineSegment(sketch, "E160", {"start": v(1295.4, 685.8) * mm, "end": v(838.2, 558.8) * mm});
            skLineSegment(sketch, "E161", {"start": v(838.2, 558.8) * mm, "end": v(1295.4, 558.8) * mm});
            skLineSegment(sketch, "E162", {"start": v(1295.4, 558.8) * mm, "end": v(1295.4, 685.8) * mm});
            skLineSegment(sketch, "E163", {"start": v(-1295.4, 685.8) * mm, "end": v(-838.2, 558.8) * mm});
            skLineSegment(sketch, "E164", {"start": v(-838.2, 558.8) * mm, "end": v(-1295.4, 558.8) * mm});
            skLineSegment(sketch, "E165", {"start": v(-1295.4, 558.8) * mm, "end": v(-1295.4, 685.8) * mm});
            skSolve(sketch);
        }
        {
            var Q0;
            Q0=qSketchRegion(id+"F27",true);
            var Q1;
            Q1=makeQuery(id+"FXyAjUxtZ6j64gG_1.boolean.opBoolean","COPY",FACE,{"derivedFrom":makeQuery(id+"FXyAjUxtZ6j64gG_1.opExtrude","SWEPT_FACE",FACE,{"disambiguationData":[OSD([sQuery(id+"FEVcK0W1Aff6NI5_1.wireOp",EDGE,"pTECiLTD-joyk-sLnn-tqEg-iIuuWTTd3Z22")])]})});
            extrude(context, id + "F28", {"entities" : qUnion([Q0]), "operationType" : NewBodyOperationType.REMOVE, "endBound" : BoundingType.THROUGH_ALL, "oppositeDirection" : true, "endBoundEntityFace" : qUnion([Q1]), "depth" : 25.4 * mm});
        }
        {
            var Q0;
            Q0=makeQuery(id+"F19.boolean.opBoolean","MERGE",FACE,{"derivedFrom":[makeQuery(id+"F1.opExtrude","SWEPT_FACE",FACE,{"disambiguationData":[OSD([sQuery(id+"F0.wireOp",EDGE,"E0.rect.left")])]}),makeQuery(id+"F19.opExtrude","SWEPT_FACE",FACE,{"disambiguationData":[OSD([sQuery(id+"F18.wireOp",EDGE,"E79")])]})]});
            var sketch = newSketch(context, id + "F29", { "sketchPlane" : qUnion([Q0])});
            skLineSegment(sketch, "E166", {"start": v(0, 0) * mm, "end": v(-7324.73, 0) * mm, "construction": true});
            skCircle(sketch, "E167", {"center": v(-2092.33, 330.2) * mm, "radius": 330.2 * mm});
            skCircle(sketch, "E168", {"center": v(-3006.72, 330.2) * mm, "radius": 330.2 * mm});
            skLineSegment(sketch, "E169", {"start": v(-3006.72, 330.2) * mm, "end": v(-2092.33, 330.2) * mm, "construction": true});
            skLineSegment(sketch, "E170", {"start": v(-2549.53, 330.2) * mm, "end": v(-2549.53, 0) * mm, "construction": true});
            skSolve(sketch);
        }
        {
            var Q0;
            Q0 = qSketchRegion(id + "F29", true);
            extrude(context, id + "F30", {"entities" : qUnion([Q0]), "operationType" : NewBodyOperationType.ADD, "oppositeDirection" : true, "depth" : 381 * mm});
        }
        {
            var Q0;
            Q0=makeQuery(id+"F30.opExtrude","CAP_FACE",FACE,{"disambiguationData":[OSD([sQuery(id+"F29.wireOp",EDGE,"E168")])],"isStart":true});
            var Q1;
            Q1=makeQuery(id+"F30.opExtrude","CAP_FACE",FACE,{"disambiguationData":[OSD([sQuery(id+"F29.wireOp",EDGE,"E167")])],"isStart":true});
            var Q2;
            Q2=makeQuery(id+"F19.boolean.opBoolean","MERGE",FACE,{"derivedFrom":[makeQuery(id+"F1.opExtrude","SWEPT_FACE",FACE,{"disambiguationData":[OSD([sQuery(id+"F0.wireOp",EDGE,"E0.rect.right")])]}),makeQuery(id+"F19.opExtrude","SWEPT_FACE",FACE,{"disambiguationData":[OSD([sQuery(id+"F18.wireOp",EDGE,"E82")])]})]});
            extrude(context, id + "F31", {"entities" : qUnion([Q0, Q1]), "operationType" : NewBodyOperationType.ADD, "endBound" : BoundingType.UP_TO_SURFACE, "oppositeDirection" : true, "endBoundEntityFace" : qUnion([Q2]), "depth" : 25.4 * mm, "hasSecondDirection" : true, "secondDirectionOppositeDirection" : true, "secondDirectionDepth" : 2209.8 * mm});
        }
    });
